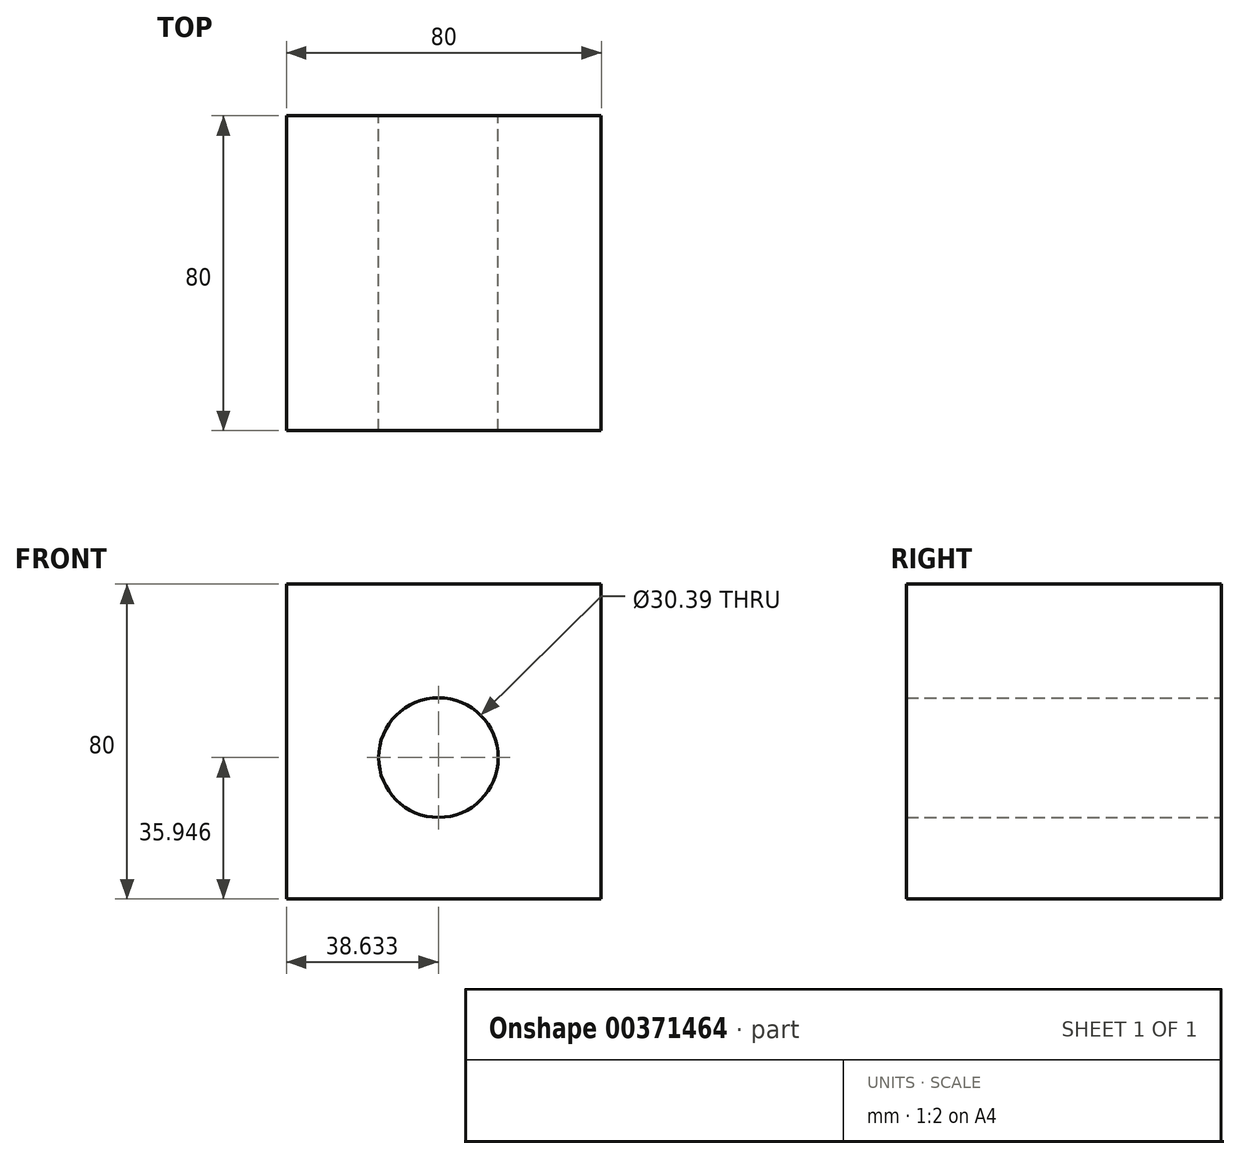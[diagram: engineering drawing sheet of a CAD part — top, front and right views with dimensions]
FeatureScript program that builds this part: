
annotation { "Feature Type Name" : "Feature", "Feature Type Description" : "" }
export const myFeature = defineFeature(function(context is Context, id is Id, definition is map)
    precondition{}
    {
        {
            var Q0;
            Q0=qCreatedBy(makeId("Top.planeOp"),FACE);
            var sketch = newSketch(context, id + "F0", { "sketchPlane" : qUnion([Q0])});
            skLineSegment(sketch, "E0.bottom", {"start": v(-3042.53, 1046.33) * mm, "end": v(3031.86, 1046.33) * mm});
            skLineSegment(sketch, "E0.top", {"start": v(-3042.53, -985.67) * mm, "end": v(3031.86, -985.67) * mm});
            skLineSegment(sketch, "E0.left", {"start": v(-3042.53, 1046.33) * mm, "end": v(-3042.53, -985.67) * mm});
            skLineSegment(sketch, "E0.right", {"start": v(3031.86, 1046.33) * mm, "end": v(3031.86, -985.67) * mm});
            skLineSegment(sketch, "E1.bottom", {"start": v(-67.36, 87.16) * mm, "end": v(12.64, 87.16) * mm});
            skLineSegment(sketch, "E1.top", {"start": v(-67.36, 7.16) * mm, "end": v(12.64, 7.16) * mm});
            skLineSegment(sketch, "E1.left", {"start": v(-67.36, 87.16) * mm, "end": v(-67.36, 7.16) * mm});
            skLineSegment(sketch, "E1.right", {"start": v(12.64, 87.16) * mm, "end": v(12.64, 7.16) * mm});
            skSolve(sketch);
        }
        {
            var Q0;
            Q0=makeQuery(id+"F0.imprint","IMPRINT",FACE,{"disambiguationData":[TD([[makeQuery(id+"F0.imprint","IMPRINT",EDGE,{"derivedFrom":sQuery(id+"F0.wireOp",EDGE,"E1.bottom")}),-1.0]])]});
            extrude(context, id + "F1", {"entities" : qUnion([Q0]), "depth" : 80 * mm});
        }
        {
            var Q0;
            Q0=makeQuery(id+"F1.opExtrude","SWEPT_FACE",FACE,{"disambiguationData":[OSD([sQuery(id+"F0.wireOp",EDGE,"E1.bottom")])]});
            var sketch = newSketch(context, id + "F2", { "sketchPlane" : qUnion([Q0])});
            skCircle(sketch, "E2", {"center": v(23.61, 65.02) * mm, "radius": 5.42 * mm});
            skCircle(sketch, "E3", {"center": v(23.61, 65.02) * mm, "radius": 4.9 * mm});
            skCircle(sketch, "E4", {"center": v(28.73, 35.95) * mm, "radius": 15.2 * mm});
            skSolve(sketch);
        }
        {
            var Q0;
            Q0=makeQuery(id+"F2.imprint","IMPRINT",FACE,{"disambiguationData":[TD([[makeQuery(id+"F2.imprint","IMPRINT",EDGE,{"derivedFrom":sQuery(id+"F2.wireOp",EDGE,"E4")}),1.0]])]});
            extrude(context, id + "F3", {"entities" : qUnion([Q0]), "operationType" : NewBodyOperationType.REMOVE, "endBound" : BoundingType.THROUGH_ALL, "oppositeDirection" : true, "depth" : 25 * mm});
        }
    });
